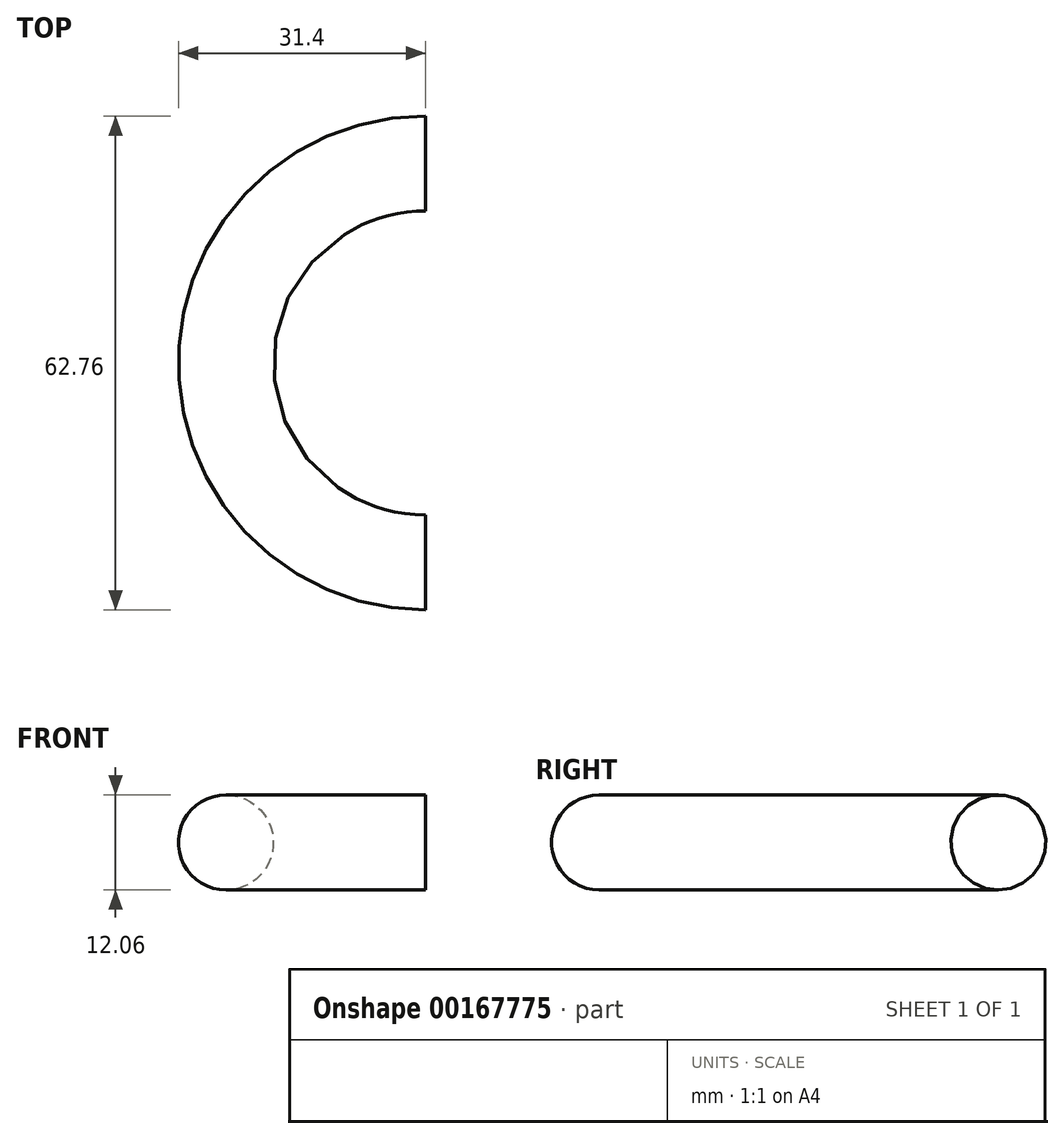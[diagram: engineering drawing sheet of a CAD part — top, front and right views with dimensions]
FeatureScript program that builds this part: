
annotation { "Feature Type Name" : "Feature", "Feature Type Description" : "" }
export const myFeature = defineFeature(function(context is Context, id is Id, definition is map)
    precondition{}
    {
        {
            var Q0;
            Q0=qCreatedBy(makeId("Top.planeOp"),FACE);
            var sketch = newSketch(context, id + "F0", { "sketchPlane" : qUnion([Q0])});
            skArc(sketch, "E0", {"start": v(-0.02, -25.4) * mm, "mid": v(25.4, -0.02) * mm, "end": v(0.03, 25.4) * mm});
            skSolve(sketch);
        }
        {
            var Q0;
            Q0=qCreatedBy(makeId("Right.planeOp"),FACE);
            var sketch = newSketch(context, id + "F1", { "sketchPlane" : qUnion([Q0])});
            skCircle(sketch, "E1", {"center": v(25.35, 0) * mm, "radius": 6.03 * mm});
            skSolve(sketch);
        }
        {
            var Q0;
            Q0=makeQuery(id+"F1.imprint","IMPRINT",FACE,{"disambiguationData":[TD([[makeQuery(id+"F1.imprint","IMPRINT",EDGE,{"derivedFrom":sQuery(id+"F1.wireOp",EDGE,"E1")}),1.0]])]});
            var Q1;
            Q1=sQuery(id+"F0.wireOp",EDGE,"E0");
            sweep(context, id + "F2", {"profiles" : qUnion([Q0]), "path" : qUnion([Q1])});
        }
    });
